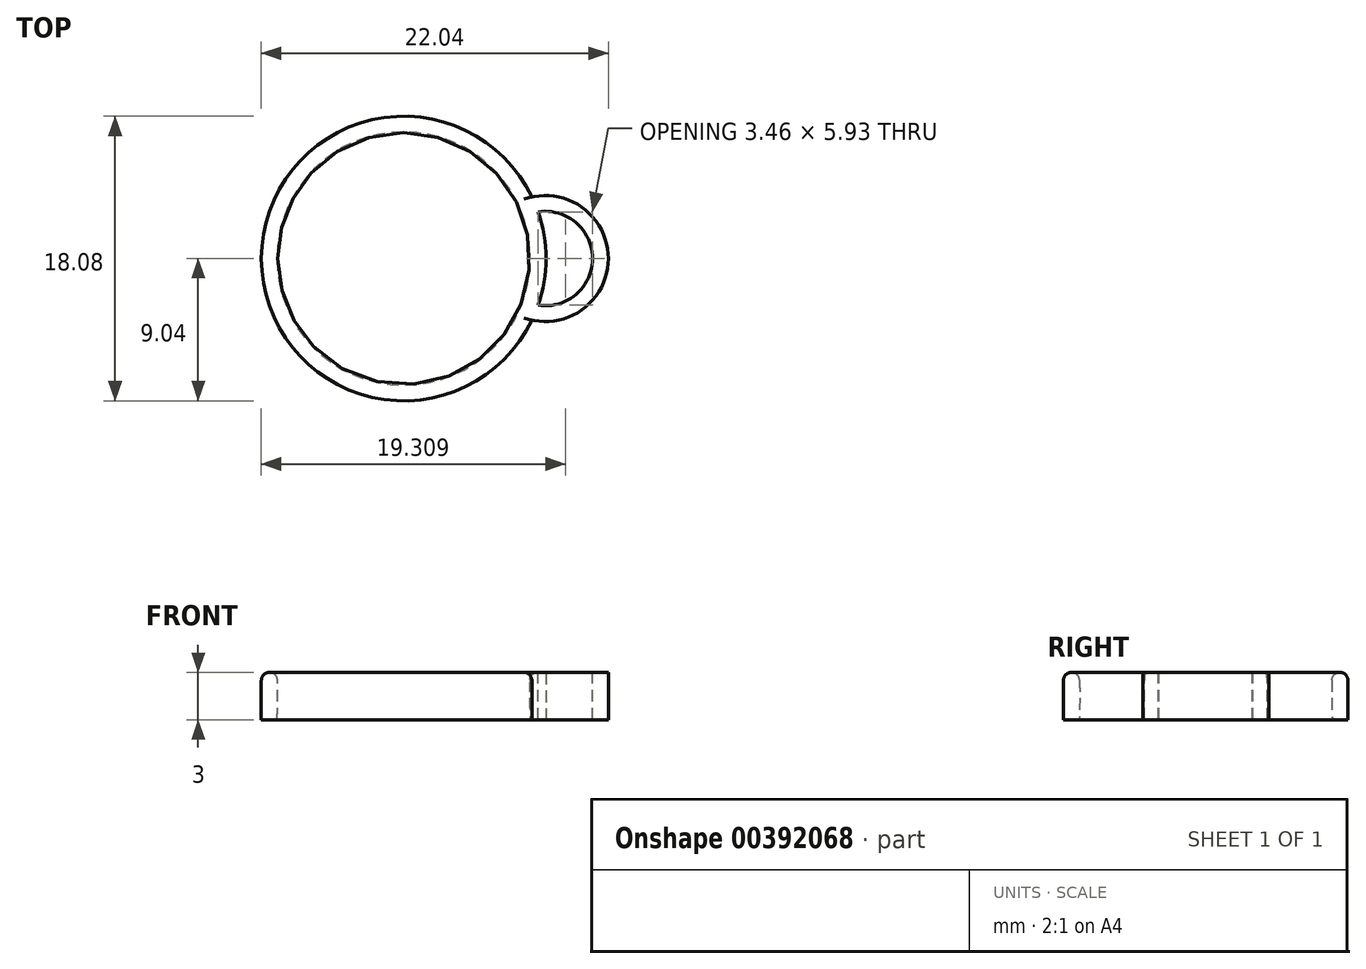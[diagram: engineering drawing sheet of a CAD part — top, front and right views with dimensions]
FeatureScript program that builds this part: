
annotation { "Feature Type Name" : "Feature", "Feature Type Description" : "" }
export const myFeature = defineFeature(function(context is Context, id is Id, definition is map)
    precondition{}
    {
        {
            assignVariable(context, id + "F0", {"name" : "RingWidth", "anyValue" : 3 * mm});
        }
        {
            var Q0;
            Q0=qCreatedBy(makeId("Front.planeOp"),FACE);
            var sketch = newSketch(context, id + "F1", { "sketchPlane" : qUnion([Q0])});
            skLineSegment(sketch, "E0", {"start": v(-9.04, 1.5) * mm, "end": v(-9.04, -1.5) * mm});
            skLineSegment(sketch, "E1", {"start": v(-9.04, -1.5) * mm, "end": v(-8.04, -1.5) * mm});
            skLineSegment(sketch, "E2", {"start": v(-9.04, 1.5) * mm, "end": v(-8.04, 1.5) * mm});
            skArc(sketch, "E3", {"start": v(-8.04, -1.5) * mm, "mid": v(-8, 0) * mm, "end": v(-8.04, 1.5) * mm});
            skLineSegment(sketch, "E4", {"start": v(-27.68, 0) * mm, "end": v(20.98, 0) * mm, "construction": true});
            skLineSegment(sketch, "E5", {"start": v(0, -9.9) * mm, "end": v(0, 28.92) * mm, "construction": true});
            skSolve(sketch);
        }
        {
            var Q0;
            Q0=makeQuery(id+"F1.imprint","IMPRINT",FACE,{"disambiguationData":[TD([[makeQuery(id+"F1.imprint","IMPRINT",EDGE,{"derivedFrom":sQuery(id+"F1.wireOp",EDGE,"E0")}),1.0]])]});
            var Q1;
            Q1=sQuery(id+"F1.wireOp",EDGE,"E5");
            revolve(context, id + "F2", {"entities" : qUnion([Q0]), "axis" : qUnion([Q1]), "revolveType" : RevolveType.FULL});
        }
        {
            var Q0;
            Q0=qCreatedBy(makeId("Top.planeOp"),FACE);
            var sketch = newSketch(context, id + "F3", { "sketchPlane" : qUnion([Q0])});
            skLineSegment(sketch, "E6", {"start": v(17.23, 0) * mm, "end": v(8.66, 0) * mm, "construction": true});
            skPoint(sketch, "E6.endSnap0", {"position": v(8.66, 0) * mm});
            skArc(sketch, "E7", {"start": v(8.15, -3.9) * mm, "mid": v(13, 0) * mm, "end": v(8.15, 3.9) * mm});
            skLineSegment(sketch, "E8", {"start": v(13.5, 0) * mm, "end": v(13.5, 0) * mm});
            skArc(sketch, "E9", {"start": v(8.54, -2.96) * mm, "mid": v(12, 0) * mm, "end": v(8.54, 2.96) * mm});
            skCircle(sketch, "E10.0", {"center": v(0, 0) * mm, "radius": 9.04 * mm});
            skSolve(sketch);
        }
        {
            var Q0;
            {var subQ0=sQuery(id+"F3.wireOp",EDGE,"E7");Q0=makeQuery(id+"F3.imprint","IMPRINT",FACE,{"disambiguationData":[TD([[makeQuery(id+"F3.imprint","IMPRINT",EDGE,{"derivedFrom":subQ0}),1.0]])]});}
            extrude(context, id + "F4", {"entities" : qUnion([Q0]), "operationType" : NewBodyOperationType.ADD, "oppositeDirection" : true, "depth" : getVariable(context, 'RingWidth') / 2});
        }
        {
            var Q0;
            Q0=makeQuery(id+"F4.opExtrude","CAP_FACE",FACE,{"disambiguationData":[OSD([sQuery(id+"F3.wireOp",EDGE,"E7"),sQuery(id+"F3.wireOp",EDGE,"E9"),sQuery(id+"F3.wireOp",EDGE,"E10.0")])],"isStart":true});
            extrude(context, id + "F5", {"entities" : qUnion([Q0]), "operationType" : NewBodyOperationType.ADD, "depth" : getVariable(context, 'RingWidth') / 2});
        }
        {
            var Q0;
            {var subQ0=sQuery(id+"F3.wireOp",EDGE,"E7");var subQ1=sQuery(id+"F1.wireOp",EDGE,"E2");var subQ2=sQuery(id+"F1.wireOp",EDGE,"E0");Q0=makeQuery(id+"F5.boolean.opBoolean","SPLIT",EDGE,{"disambiguationData":[TD([makeQuery(id+"F4.opExtrude","SWEPT_FACE",FACE,{"disambiguationData":[OSD([subQ0])]})])],"derivedFrom":makeQuery(id+"F2.opRevolve","SWEPT_EDGE",EDGE,{"disambiguationData":[OSD([subQ2,subQ1])]})});}
            var Q1;
            Q1=makeQuery(id+"F2.opRevolve","SWEPT_EDGE",EDGE,{"disambiguationData":[OSD([sQuery(id+"F1.wireOp",EDGE,"E2"),sQuery(id+"F1.wireOp",EDGE,"E3")])]});
            fillet(context, id + "F6", {"entities" : qUnion([Q0, Q1]), "radius" : 0.5 * mm, "tangentPropagation" : true, "allowEdgeOverflow" : false});
        }
    });
